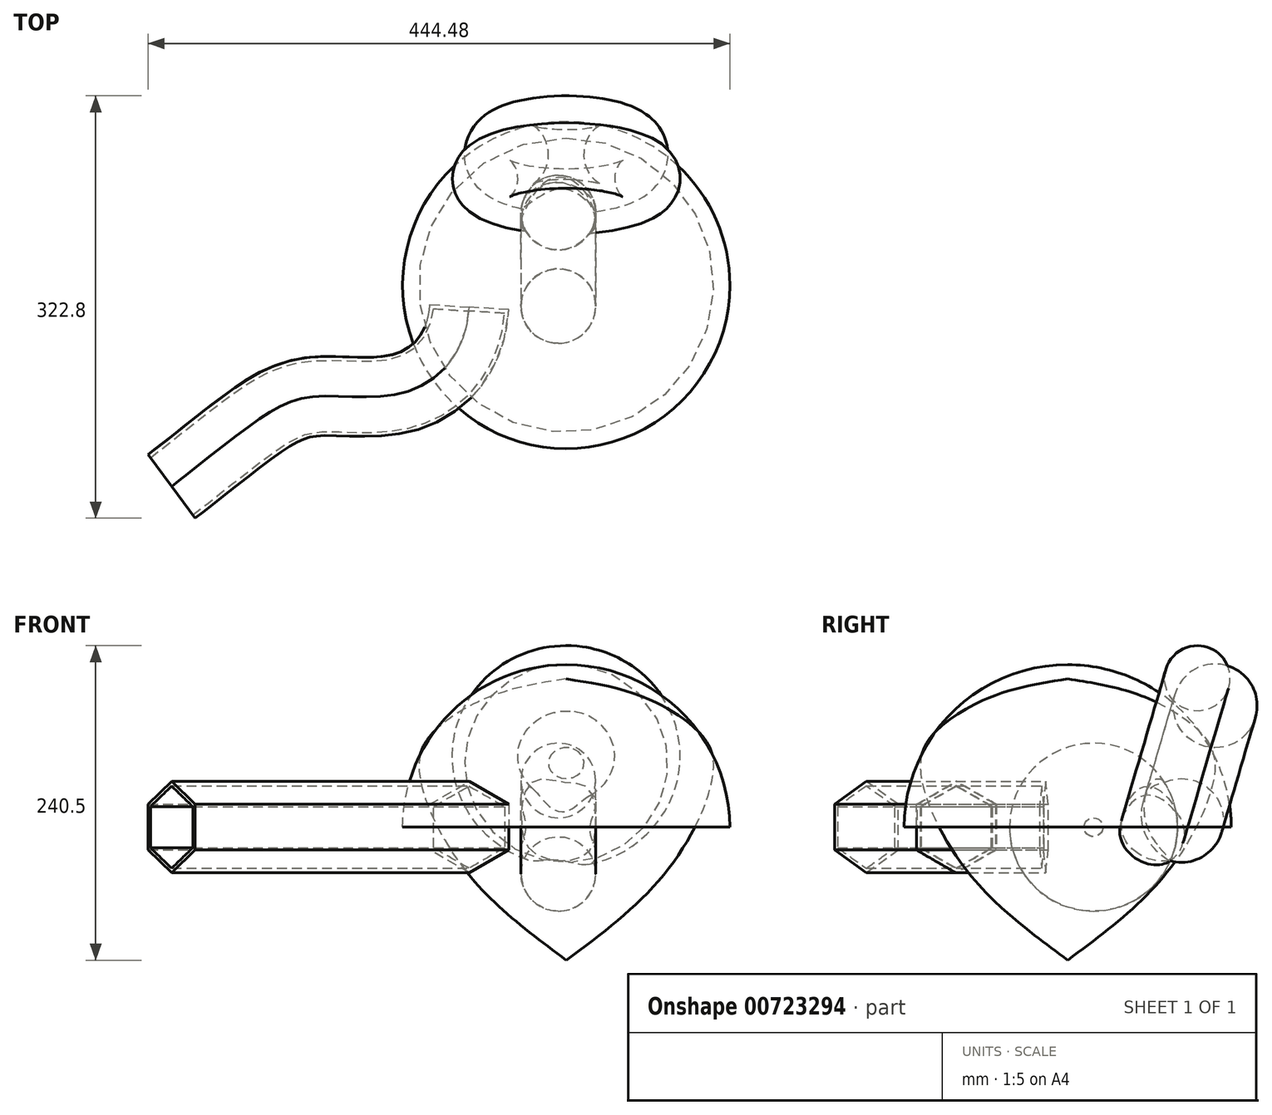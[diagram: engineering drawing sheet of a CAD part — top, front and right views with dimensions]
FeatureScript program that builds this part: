
annotation { "Feature Type Name" : "Feature", "Feature Type Description" : "" }
export const myFeature = defineFeature(function(context is Context, id is Id, definition is map)
    precondition{}
    {
        {
            var Q0;
            Q0=qCreatedBy(makeId("Right.planeOp"),FACE);
            var sketch = newSketch(context, id + "F0", { "sketchPlane" : qUnion([Q0])});
            skLineSegment(sketch, "E0", {"start": v(0, 113.31) * mm, "end": v(0, -133) * mm});
            skFitSpline(sketch, "E1", {"points": [v(0, 113.31) * mm, v(56.93, 100.26) * mm, v(102.85, 71.04) * mm, v(112.25, 41.3) * mm, v(77.29, -32.8) * mm, v(0, -101.68) * mm], "startDerivative": vector(298.46, -45.65) * mm, "endDerivative": vector(-328.3, -243.63) * mm});
            skSolve(sketch);
        }
        {
            var Q0;
            {var subQ0=sQuery(id+"F0.wireOp",EDGE,"E1");Q0=makeQuery(id+"F0.imprint","IMPRINT",FACE,{"disambiguationData":[TD([[makeQuery(id+"F0.imprint","IMPRINT",EDGE,{"derivedFrom":subQ0}),-1.0]])]});}
            var Q1;
            Q1=sQuery(id+"F0.wireOp",EDGE,"E0");
            revolve(context, id + "F1", {"surfaceOperationType" : NewSurfaceOperationType.NEW, "entities" : qUnion([Q0]), "axis" : qUnion([Q1]), "revolveType" : RevolveType.FULL});
        }
        {
            var Q0;
            Q0=qCreatedBy(makeId("Right.planeOp"),FACE);
            var sketch = newSketch(context, id + "F2", { "sketchPlane" : qUnion([Q0])});
            skLineSegment(sketch, "E2", {"start": v(0, 124.26) * mm, "end": v(0, -125.74) * mm});
            skArc(sketch, "E3", {"start": v(0, -125.74) * mm, "mid": v(125, -0.74) * mm, "end": v(0, 124.26) * mm});
            skLineSegment(sketch, "E4", {"start": v(0, 0) * mm, "end": v(125, 0) * mm});
            skSolve(sketch);
        }
        {
            var Q0;
            {var subQ3=sQuery(id+"F2.wireOp",EDGE,"E4");Q0=makeQuery(id+"F2.imprint","IMPRINT",FACE,{"disambiguationData":[TD([[makeQuery(id+"F2.imprint","IMPRINT",EDGE,{"derivedFrom":subQ3}),-1.0]])]});}
            var Q1;
            Q1=sQuery(id+"F2.wireOp",EDGE,"E2");
            revolve(context, id + "F3", {"surfaceOperationType" : NewSurfaceOperationType.NEW, "entities" : qUnion([Q0]), "axis" : qUnion([Q1]), "revolveType" : RevolveType.FULL});
        }
        {
            var Q0;
            Q0=qCreatedBy(makeId("Right.planeOp"),FACE);
            var sketch = newSketch(context, id + "F4", { "sketchPlane" : qUnion([Q0])});
            skLineSegment(sketch, "E5", {"start": v(0, 97.72) * mm, "end": v(0, -106.66) * mm});
            skCircle(sketch, "E6", {"center": v(86.98, 5.14) * mm, "radius": 32 * mm});
            skLineSegment(sketch, "E7", {"start": v(-73.55, 99.95) * mm, "end": v(180.46, 25.27) * mm});
            skCircle(sketch, "E8", {"center": v(99.07, 113.82) * mm, "radius": 25 * mm});
            skLineSegment(sketch, "E9", {"start": v(99.07, 113.82) * mm, "end": v(124.07, 113.82) * mm});
            skSolve(sketch);
        }
        {
            var Q0;
            Q0=makeQuery(id+"F4.imprint","IMPRINT",FACE,{"disambiguationData":[TD([[makeQuery(id+"F4.imprint","IMPRINT",EDGE,{"derivedFrom":sQuery(id+"F4.wireOp",EDGE,"E8")}),1.0]])]});
            var Q1;
            Q1=makeQuery(id+"F4.imprint","IMPRINT",FACE,{"disambiguationData":[TD([[makeQuery(id+"F4.imprint","IMPRINT",EDGE,{"derivedFrom":sQuery(id+"F4.wireOp",EDGE,"E6")}),1.0]])]});
            var Q2;
            Q2=sQuery(id+"F4.wireOp",EDGE,"E7");
            revolve(context, id + "F5", {"surfaceOperationType" : NewSurfaceOperationType.NEW, "entities" : qUnion([Q0, Q1]), "axis" : qUnion([Q2]), "revolveType" : RevolveType.FULL});
        }
        {
            var Q0;
            Q0=qCreatedBy(makeId("Top.planeOp"),FACE);
            var sketch = newSketch(context, id + "F6", { "sketchPlane" : qUnion([Q0])});
            skLineSegment(sketch, "E10", {"start": v(128.44, 19.71) * mm, "end": v(-138.82, 19.71) * mm});
            skCircle(sketch, "E11", {"center": v(-6.02, -15.98) * mm, "radius": 28.5 * mm});
            skSolve(sketch);
        }
        {
            var Q0;
            Q0 = qSketchRegion(id + "F6", true);
            var Q1;
            Q1=sQuery(id+"F6.wireOp",EDGE,"E10");
            revolve(context, id + "F7", {"operationType" : NewBodyOperationType.REMOVE, "surfaceOperationType" : NewSurfaceOperationType.NEW, "entities" : qUnion([Q0]), "axis" : qUnion([Q1]), "revolveType" : RevolveType.FULL, "oppositeDirection" : true});
        }
        {
            var Q0;
            Q0=qCreatedBy(makeId("Top.planeOp"),FACE);
            var sketch = newSketch(context, id + "F8", { "sketchPlane" : qUnion([Q0])});
            skFitSpline(sketch, "E12", {"points": [v(-74.03, -16.79) * mm, v(-124.4, -82.17) * mm, v(-194.85, -85.38) * mm, v(-244.12, -109.18) * mm, v(-301.48, -153.76) * mm], "startDerivative": vector(-26.95, -411.44) * mm, "endDerivative": vector(-122.59, -90.86) * mm});
            skSolve(sketch);
        }
        {
            var Q0;
            Q0=sQuery(id+"F8.wireOp",VERTEX,"E12.end");
            var Q1;
            Q1=sQuery(id+"F8.wireOp",EDGE,"E12");
            cPlane(context, id + "F9", {"entities" : qUnion([Q0, Q1]), "cplaneType" : CPlaneType.CURVE_POINT, "offset" : 25 * mm, "width" : 150 * mm, "height" : 150 * mm});
        }
        {
            var Q0;
            Q0=qCreatedBy(id+"F9.planeOp",FACE);
            var sketch = newSketch(context, id + "F10", { "sketchPlane" : qUnion([Q0])});
            skCircle(sketch, "E13.cCircle", {"center": v(-56, 0) * mm, "radius": 30.22 * mm, "construction": true});
            skLineSegment(sketch, "E13.0", {"start": v(-86.22, -17.45) * mm, "end": v(-86.22, 17.45) * mm});
            skLineSegment(sketch, "E13.1", {"start": v(-86.22, 17.45) * mm, "end": v(-56, 34.9) * mm});
            skLineSegment(sketch, "E13.2", {"start": v(-56, 34.9) * mm, "end": v(-25.77, 17.45) * mm});
            skLineSegment(sketch, "E13.3", {"start": v(-25.77, 17.45) * mm, "end": v(-25.77, -17.45) * mm});
            skLineSegment(sketch, "E13.4", {"start": v(-25.77, -17.45) * mm, "end": v(-56, -34.9) * mm});
            skLineSegment(sketch, "E13.5", {"start": v(-56, -34.9) * mm, "end": v(-86.22, -17.45) * mm});
            skPoint(sketch, "E13.0.midPoint", {"position": v(-86.22, 0) * mm});
            skSolve(sketch);
        }
        {
            var Q0;
            Q0=makeQuery(id+"F10.imprint","IMPRINT",FACE,{"disambiguationData":[TD([[makeQuery(id+"F10.imprint","IMPRINT",EDGE,{"derivedFrom":sQuery(id+"F10.wireOp",EDGE,"E13.0")}),-1.0]])]});
            var Q1;
            Q1=sQuery(id+"F8.wireOp",EDGE,"E12");
            sweep(context, id + "F11", {"profiles" : qUnion([Q0]), "path" : qUnion([Q1])});
        }
        {
            var Q0;
            Q0=makeQuery(id+"F11.opSweep","CAP_FACE",FACE,{"disambiguationData":[OSD([sQuery(id+"F8.wireOp",VERTEX,"E12.end"),sQuery(id+"F10.wireOp",EDGE,"E13.0"),sQuery(id+"F10.wireOp",EDGE,"E13.1"),sQuery(id+"F10.wireOp",EDGE,"E13.2"),sQuery(id+"F10.wireOp",EDGE,"E13.3"),sQuery(id+"F10.wireOp",EDGE,"E13.4"),sQuery(id+"F10.wireOp",EDGE,"E13.5")])],"isStart":true});
            shell(context, id + "F12", {"entities" : qUnion([Q0]), "thickness" : 3 * mm});
        }
    });
